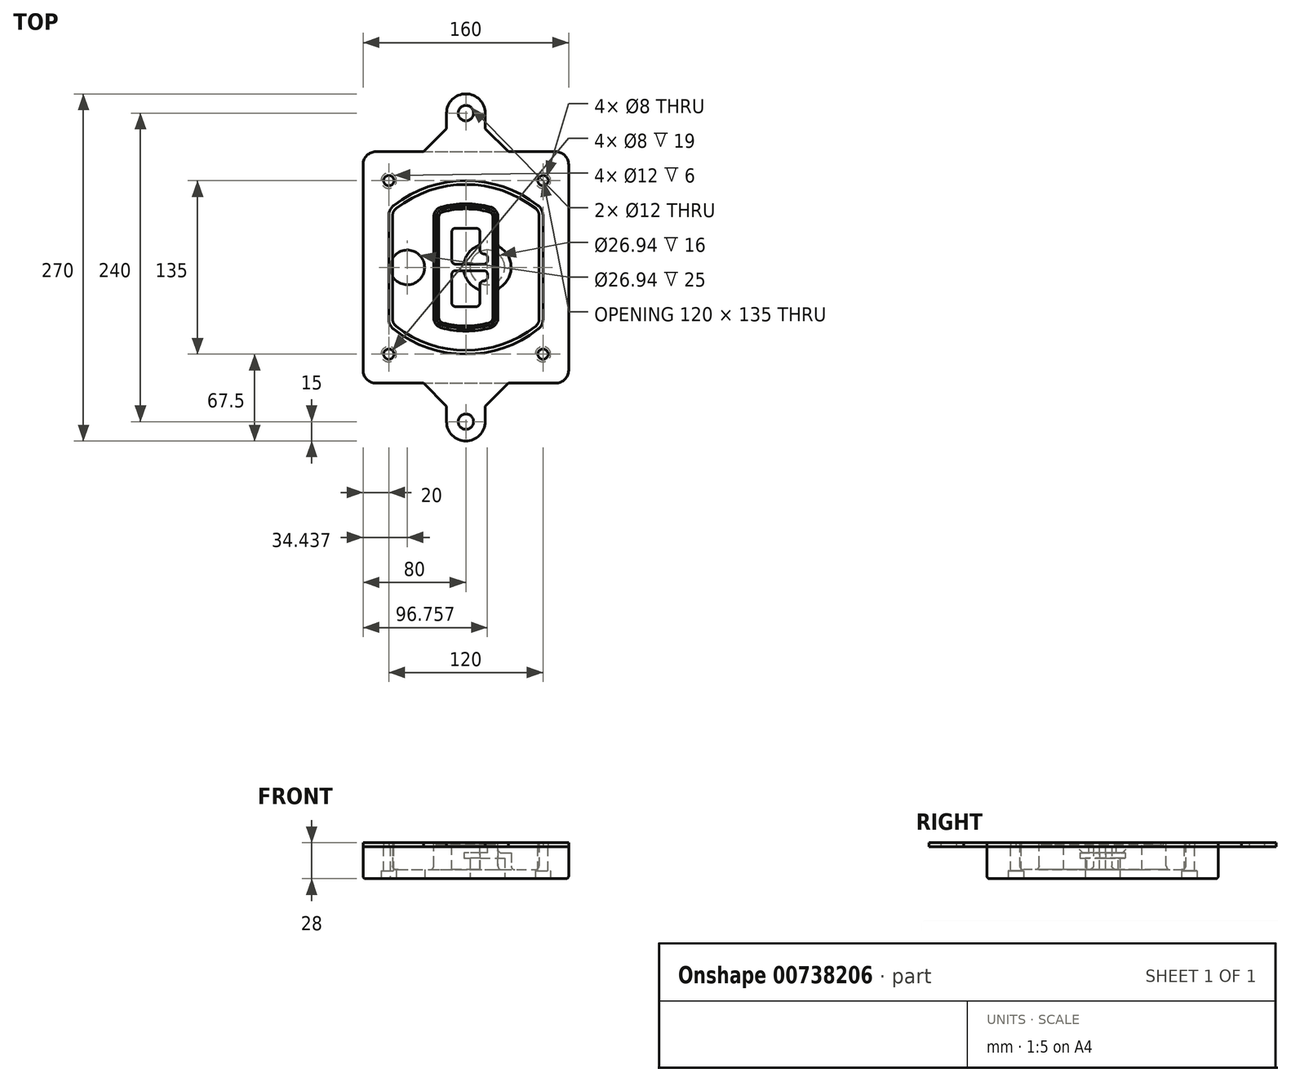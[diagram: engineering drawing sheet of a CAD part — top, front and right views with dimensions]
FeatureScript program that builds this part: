
annotation { "Feature Type Name" : "Feature", "Feature Type Description" : "" }
export const myFeature = defineFeature(function(context is Context, id is Id, definition is map)
    precondition{}
    {
        {
            var Q0;
            Q0=qCreatedBy(makeId("Top.planeOp"),FACE);
            var sketch = newSketch(context, id + "F0", { "sketchPlane" : qUnion([Q0])});
            skPoint(sketch, "E0.rect.middle", {"position": v(0, 0) * mm});
            skLineSegment(sketch, "E1.bottom", {"start": v(-70, -90) * mm, "end": v(70, -90) * mm});
            skLineSegment(sketch, "E1.top", {"start": v(-70, 90) * mm, "end": v(70, 90) * mm});
            skLineSegment(sketch, "E1.left", {"start": v(-80, -80) * mm, "end": v(-80, 80) * mm});
            skLineSegment(sketch, "E1.right", {"start": v(80, -80) * mm, "end": v(80, 80) * mm});
            skLineSegment(sketch, "E2", {"start": v(-80, 90) * mm, "end": v(80, -90) * mm, "construction": true});
            skLineSegment(sketch, "E3", {"start": v(80, 90) * mm, "end": v(-80, -90) * mm, "construction": true});
            skCircle(sketch, "E4", {"center": v(-60, 67.5) * mm, "radius": 4 * mm});
            skCircle(sketch, "E5", {"center": v(60, 67.5) * mm, "radius": 4 * mm});
            skCircle(sketch, "E6", {"center": v(60, -67.5) * mm, "radius": 4 * mm});
            skCircle(sketch, "E7", {"center": v(-60, -67.5) * mm, "radius": 4 * mm});
            skLineSegment(sketch, "E8", {"start": v(-60, 67.5) * mm, "end": v(60, 67.5) * mm, "construction": true});
            skLineSegment(sketch, "E9", {"start": v(60, 67.5) * mm, "end": v(60, -67.5) * mm, "construction": true});
            skLineSegment(sketch, "E10", {"start": v(60, -67.5) * mm, "end": v(-60, -67.5) * mm, "construction": true});
            skLineSegment(sketch, "E11", {"start": v(-60, -67.5) * mm, "end": v(-60, 67.5) * mm, "construction": true});
            skLineSegment(sketch, "E12", {"start": v(-60, 40.3) * mm, "end": v(-60, -40.3) * mm});
            skLineSegment(sketch, "E13", {"start": v(60, 40.3) * mm, "end": v(60, -40.3) * mm});
            skArc(sketch, "E14", {"start": v(56.15, 48.18) * mm, "mid": v(0, 67.5) * mm, "end": v(-56.15, 48.18) * mm});
            skArc(sketch, "E15", {"start": v(-56.15, -48.18) * mm, "mid": v(0, -67.5) * mm, "end": v(56.15, -48.18) * mm});
            skLineSegment(sketch, "E16", {"start": v(-60, 0) * mm, "end": v(60, 0) * mm, "construction": true});
            skPoint(sketch, "E17.visualSharp", {"position": v(-60, -45) * mm});
            skArc(sketch, "E17.filletArc", {"start": v(-60, -40.3) * mm, "mid": v(-58.99, -44.68) * mm, "end": v(-56.15, -48.18) * mm});
            skPoint(sketch, "E18.visualSharp", {"position": v(-60, 45) * mm});
            skArc(sketch, "E18.filletArc", {"start": v(-56.15, 48.18) * mm, "mid": v(-58.99, 44.68) * mm, "end": v(-60, 40.3) * mm});
            skPoint(sketch, "E19.visualSharp", {"position": v(60, 45) * mm});
            skArc(sketch, "E19.filletArc", {"start": v(60, 40.3) * mm, "mid": v(58.99, 44.68) * mm, "end": v(56.15, 48.18) * mm});
            skPoint(sketch, "E20.visualSharp", {"position": v(60, -45) * mm});
            skArc(sketch, "E20.filletArc", {"start": v(56.15, -48.18) * mm, "mid": v(58.99, -44.68) * mm, "end": v(60, -40.3) * mm});
            skPoint(sketch, "E21.visualSharp", {"position": v(-80, 90) * mm});
            skArc(sketch, "E21.filletArc", {"start": v(-70, 90) * mm, "mid": v(-77.07, 87.07) * mm, "end": v(-80, 80) * mm});
            skPoint(sketch, "E22.visualSharp", {"position": v(80, 90) * mm});
            skArc(sketch, "E22.filletArc", {"start": v(80, 80) * mm, "mid": v(77.07, 87.07) * mm, "end": v(70, 90) * mm});
            skPoint(sketch, "E23.visualSharp", {"position": v(80, -90) * mm});
            skArc(sketch, "E23.filletArc", {"start": v(70, -90) * mm, "mid": v(77.07, -87.07) * mm, "end": v(80, -80) * mm});
            skPoint(sketch, "E24.visualSharp", {"position": v(-80, -90) * mm});
            skArc(sketch, "E24.filletArc", {"start": v(-80, -80) * mm, "mid": v(-77.07, -87.07) * mm, "end": v(-70, -90) * mm});
            skArc(sketch, "E25.0", {"start": v(57, 40.3) * mm, "mid": v(56.3, 43.36) * mm, "end": v(54.3, 45.81) * mm});
            skLineSegment(sketch, "E25.1", {"start": v(57, 40.3) * mm, "end": v(57, -40.3) * mm});
            skArc(sketch, "E25.2", {"start": v(54.3, -45.81) * mm, "mid": v(56.3, -43.36) * mm, "end": v(57, -40.3) * mm});
            skArc(sketch, "E25.3", {"start": v(-54.3, -45.81) * mm, "mid": v(0, -64.5) * mm, "end": v(54.3, -45.81) * mm});
            skArc(sketch, "E25.4", {"start": v(-57, -40.3) * mm, "mid": v(-56.3, -43.36) * mm, "end": v(-54.3, -45.81) * mm});
            skArc(sketch, "E25.5", {"start": v(54.3, 45.81) * mm, "mid": v(0, 64.5) * mm, "end": v(-54.3, 45.81) * mm});
            skLineSegment(sketch, "E25.6", {"start": v(-57, 40.3) * mm, "end": v(-57, -40.3) * mm});
            skArc(sketch, "E25.7", {"start": v(-54.3, 45.81) * mm, "mid": v(-56.3, 43.36) * mm, "end": v(-57, 40.3) * mm});
            skArc(sketch, "E26.0", {"start": v(-58.62, 51.33) * mm, "mid": v(-62.58, 46.43) * mm, "end": v(-64, 40.3) * mm});
            skArc(sketch, "E26.1", {"start": v(58.62, 51.33) * mm, "mid": v(0, 71.5) * mm, "end": v(-58.62, 51.33) * mm});
            skArc(sketch, "E26.2", {"start": v(64, 40.3) * mm, "mid": v(62.58, 46.43) * mm, "end": v(58.62, 51.33) * mm});
            skLineSegment(sketch, "E26.3", {"start": v(64, 40.3) * mm, "end": v(64, -40.3) * mm});
            skArc(sketch, "E26.4", {"start": v(58.62, -51.33) * mm, "mid": v(62.58, -46.43) * mm, "end": v(64, -40.3) * mm});
            skLineSegment(sketch, "E26.5", {"start": v(-64, 40.3) * mm, "end": v(-64, -40.3) * mm});
            skArc(sketch, "E26.6", {"start": v(-58.62, -51.33) * mm, "mid": v(0, -71.5) * mm, "end": v(58.62, -51.33) * mm});
            skArc(sketch, "E26.7", {"start": v(-64, -40.3) * mm, "mid": v(-62.58, -46.43) * mm, "end": v(-58.62, -51.33) * mm});
            skSolve(sketch);
        }
        {
            var Q0;
            Q0=makeQuery(id+"F0.imprint","IMPRINT",FACE,{"disambiguationData":[TD([[makeQuery(id+"F0.imprint","IMPRINT",EDGE,{"derivedFrom":sQuery(id+"F0.wireOp",EDGE,"E1.bottom")}),1.0]])]});
            var Q1;
            Q1=makeQuery(id+"F0.imprint","IMPRINT",FACE,{"disambiguationData":[TD([[makeQuery(id+"F0.imprint","IMPRINT",EDGE,{"derivedFrom":sQuery(id+"F0.wireOp",EDGE,"E12")}),1.0]])]});
            var Q2;
            Q2=makeQuery(id+"F0.imprint","IMPRINT",FACE,{"disambiguationData":[TD([[makeQuery(id+"F0.imprint","IMPRINT",EDGE,{"derivedFrom":sQuery(id+"F0.wireOp",EDGE,"E25.0")}),1.0]])]});
            var Q3;
            Q3=makeQuery(id+"F0.imprint","IMPRINT",FACE,{"disambiguationData":[TD([[makeQuery(id+"F0.imprint","IMPRINT",EDGE,{"derivedFrom":sQuery(id+"F0.wireOp",EDGE,"E12")}),-1.0]])]});
            extrude(context, id + "F1", {"entities" : qUnion([Q0, Q1, Q2, Q3]), "oppositeDirection" : true, "depth" : 25 * mm});
        }
        {
            var Q0;
            Q0=makeQuery(id+"F0.imprint","IMPRINT",FACE,{"disambiguationData":[TD([[makeQuery(id+"F0.imprint","IMPRINT",EDGE,{"derivedFrom":sQuery(id+"F0.wireOp",EDGE,"E12")}),1.0]])]});
            extrude(context, id + "F2", {"entities" : qUnion([Q0]), "operationType" : NewBodyOperationType.ADD, "depth" : 3 * mm, "offsetDistance" : 25 * mm});
        }
        {
            var Q0;
            Q0=makeQuery(id+"F0.imprint","IMPRINT",FACE,{"disambiguationData":[TD([[makeQuery(id+"F0.imprint","IMPRINT",EDGE,{"derivedFrom":sQuery(id+"F0.wireOp",EDGE,"E25.0")}),1.0]])]});
            extrude(context, id + "F3", {"entities" : qUnion([Q0]), "operationType" : NewBodyOperationType.REMOVE, "oppositeDirection" : true, "depth" : 18 * mm});
        }
        {
            var Q0;
            Q0=makeQuery(id+"F2.opExtrude","CAP_FACE",FACE,{"disambiguationData":[OSD([sQuery(id+"F0.wireOp",EDGE,"E12"),sQuery(id+"F0.wireOp",EDGE,"E13"),sQuery(id+"F0.wireOp",EDGE,"E14"),sQuery(id+"F0.wireOp",EDGE,"E15"),sQuery(id+"F0.wireOp",EDGE,"E17.filletArc"),sQuery(id+"F0.wireOp",EDGE,"E18.filletArc"),sQuery(id+"F0.wireOp",EDGE,"E19.filletArc"),sQuery(id+"F0.wireOp",EDGE,"E20.filletArc"),sQuery(id+"F0.wireOp",EDGE,"E25.0"),sQuery(id+"F0.wireOp",EDGE,"E25.1"),sQuery(id+"F0.wireOp",EDGE,"E25.2"),sQuery(id+"F0.wireOp",EDGE,"E25.3"),sQuery(id+"F0.wireOp",EDGE,"E25.4"),sQuery(id+"F0.wireOp",EDGE,"E25.5"),sQuery(id+"F0.wireOp",EDGE,"E25.6"),sQuery(id+"F0.wireOp",EDGE,"E25.7")])],"isStart":false});
            var sketch = newSketch(context, id + "F4", { "sketchPlane" : qUnion([Q0])});
            skArc(sketch, "E27.0", {"start": v(-19.08, -46.97) * mm, "mid": v(0, -49.5) * mm, "end": v(19.08, -46.97) * mm});
            skArc(sketch, "E28.0", {"start": v(19.08, 46.97) * mm, "mid": v(0, 49.5) * mm, "end": v(-19.08, 46.97) * mm});
            skLineSegment(sketch, "E29", {"start": v(-25, 39.25) * mm, "end": v(-25, -39.25) * mm});
            skLineSegment(sketch, "E30", {"start": v(25, 39.25) * mm, "end": v(25, -39.25) * mm});
            skLineSegment(sketch, "E31", {"start": v(-25, 45.1) * mm, "end": v(25, 45.1) * mm, "construction": true});
            skLineSegment(sketch, "E32", {"start": v(-25, -45.1) * mm, "end": v(25, -45.1) * mm, "construction": true});
            skPoint(sketch, "E33.visualSharp", {"position": v(-25, 45.1) * mm});
            skArc(sketch, "E33.filletArc", {"start": v(-19.08, 46.97) * mm, "mid": v(-23.35, 44.11) * mm, "end": v(-25, 39.25) * mm});
            skPoint(sketch, "E34.visualSharp", {"position": v(25, 45.1) * mm});
            skArc(sketch, "E34.filletArc", {"start": v(25, 39.25) * mm, "mid": v(23.35, 44.11) * mm, "end": v(19.08, 46.97) * mm});
            skPoint(sketch, "E35.visualSharp", {"position": v(25, -45.1) * mm});
            skArc(sketch, "E35.filletArc", {"start": v(19.08, -46.97) * mm, "mid": v(23.35, -44.11) * mm, "end": v(25, -39.25) * mm});
            skPoint(sketch, "E36.visualSharp", {"position": v(-25, -45.1) * mm});
            skArc(sketch, "E36.filletArc", {"start": v(-25, -39.25) * mm, "mid": v(-23.35, -44.11) * mm, "end": v(-19.08, -46.97) * mm});
            skArc(sketch, "E37.0", {"start": v(54.3, 45.81) * mm, "mid": v(0, 64.5) * mm, "end": v(-54.3, 45.81) * mm});
            skArc(sketch, "E37.1", {"start": v(-54.3, 45.81) * mm, "mid": v(-56.3, 43.36) * mm, "end": v(-57, 40.3) * mm});
            skLineSegment(sketch, "E37.2", {"start": v(-57, 40.3) * mm, "end": v(-57, -40.3) * mm});
            skArc(sketch, "E37.3", {"start": v(-57, -40.3) * mm, "mid": v(-56.3, -43.36) * mm, "end": v(-54.3, -45.81) * mm});
            skArc(sketch, "E37.4", {"start": v(-54.3, -45.81) * mm, "mid": v(0, -64.5) * mm, "end": v(54.3, -45.81) * mm});
            skArc(sketch, "E37.5", {"start": v(54.3, -45.81) * mm, "mid": v(56.3, -43.36) * mm, "end": v(57, -40.3) * mm});
            skLineSegment(sketch, "E37.6", {"start": v(57, 40.3) * mm, "end": v(57, -40.3) * mm});
            skArc(sketch, "E37.7", {"start": v(57, 40.3) * mm, "mid": v(56.3, 43.36) * mm, "end": v(54.3, 45.81) * mm});
            skLineSegment(sketch, "E38.0", {"start": v(23, 39.25) * mm, "end": v(23, -39.25) * mm});
            skArc(sketch, "E38.1", {"start": v(18.56, -45.04) * mm, "mid": v(21.76, -42.9) * mm, "end": v(23, -39.25) * mm});
            skArc(sketch, "E38.2", {"start": v(-18.56, -45.04) * mm, "mid": v(0, -47.5) * mm, "end": v(18.56, -45.04) * mm});
            skArc(sketch, "E38.3", {"start": v(-23, -39.25) * mm, "mid": v(-21.76, -42.9) * mm, "end": v(-18.56, -45.04) * mm});
            skLineSegment(sketch, "E38.4", {"start": v(-23, 39.25) * mm, "end": v(-23, -39.25) * mm});
            skArc(sketch, "E38.5", {"start": v(23, 39.25) * mm, "mid": v(21.76, 42.9) * mm, "end": v(18.56, 45.04) * mm});
            skArc(sketch, "E38.6", {"start": v(-18.56, 45.04) * mm, "mid": v(-21.76, 42.9) * mm, "end": v(-23, 39.25) * mm});
            skArc(sketch, "E38.7", {"start": v(18.56, 45.04) * mm, "mid": v(0, 47.5) * mm, "end": v(-18.56, 45.04) * mm});
            skArc(sketch, "E39.0", {"start": v(21, 39.25) * mm, "mid": v(20.18, 41.68) * mm, "end": v(18.04, 43.1) * mm});
            skLineSegment(sketch, "E39.1", {"start": v(21, 39.25) * mm, "end": v(21, -39.25) * mm});
            skArc(sketch, "E39.2", {"start": v(18.04, -43.1) * mm, "mid": v(20.18, -41.68) * mm, "end": v(21, -39.25) * mm});
            skArc(sketch, "E39.3", {"start": v(-18.04, -43.1) * mm, "mid": v(0, -45.5) * mm, "end": v(18.04, -43.1) * mm});
            skArc(sketch, "E39.4", {"start": v(-21, -39.25) * mm, "mid": v(-20.18, -41.68) * mm, "end": v(-18.04, -43.1) * mm});
            skArc(sketch, "E39.5", {"start": v(18.04, 43.1) * mm, "mid": v(0, 45.5) * mm, "end": v(-18.04, 43.1) * mm});
            skLineSegment(sketch, "E39.6", {"start": v(-21, 39.25) * mm, "end": v(-21, -39.25) * mm});
            skArc(sketch, "E39.7", {"start": v(-18.04, 43.1) * mm, "mid": v(-20.18, 41.68) * mm, "end": v(-21, 39.25) * mm});
            skLineSegment(sketch, "E40", {"start": v(-25, 0) * mm, "end": v(25, 0) * mm, "construction": true});
            skLineSegment(sketch, "E41", {"start": v(-11, 5.5) * mm, "end": v(-11, 27.5) * mm});
            skLineSegment(sketch, "E42", {"start": v(-8, 30.5) * mm, "end": v(8, 30.5) * mm});
            skLineSegment(sketch, "E43", {"start": v(11, 27.5) * mm, "end": v(11, 13.5) * mm});
            skLineSegment(sketch, "E44", {"start": v(14, 10.5) * mm, "end": v(14, 10.5) * mm});
            skLineSegment(sketch, "E45", {"start": v(17, 7.5) * mm, "end": v(17, 5.5) * mm});
            skLineSegment(sketch, "E46", {"start": v(14, 2.5) * mm, "end": v(-8, 2.5) * mm});
            skPoint(sketch, "E47.visualSharp", {"position": v(-11, 30.5) * mm});
            skArc(sketch, "E47.filletArc", {"start": v(-8, 30.5) * mm, "mid": v(-10.12, 29.62) * mm, "end": v(-11, 27.5) * mm});
            skPoint(sketch, "E48.visualSharp", {"position": v(11, 30.5) * mm});
            skArc(sketch, "E48.filletArc", {"start": v(11, 27.5) * mm, "mid": v(10.12, 29.62) * mm, "end": v(8, 30.5) * mm});
            skPoint(sketch, "E49.visualSharp", {"position": v(11, 10.5) * mm});
            skArc(sketch, "E49.filletArc", {"start": v(11, 13.5) * mm, "mid": v(11.88, 11.38) * mm, "end": v(14, 10.5) * mm});
            skPoint(sketch, "E50.visualSharp", {"position": v(17, 10.5) * mm});
            skArc(sketch, "E50.filletArc", {"start": v(17, 7.5) * mm, "mid": v(16.12, 9.62) * mm, "end": v(14, 10.5) * mm});
            skPoint(sketch, "E51.visualSharp", {"position": v(17, 2.5) * mm});
            skArc(sketch, "E51.filletArc", {"start": v(14, 2.5) * mm, "mid": v(16.12, 3.38) * mm, "end": v(17, 5.5) * mm});
            skPoint(sketch, "E52.visualSharp", {"position": v(-11, 2.5) * mm});
            skArc(sketch, "E52.filletArc", {"start": v(-11, 5.5) * mm, "mid": v(-10.12, 3.38) * mm, "end": v(-8, 2.5) * mm});
            skLineSegment(sketch, "E53.0.MirrorCS", {"start": v(14, -2.5) * mm, "end": v(-8, -2.5) * mm});
            skArc(sketch, "E54.0.MirrorCS", {"start": v(-11, -5.5) * mm, "mid": v(-10.12, -3.38) * mm, "end": v(-8, -2.5) * mm});
            skLineSegment(sketch, "E55.0.MirrorCS", {"start": v(-11, -5.5) * mm, "end": v(-11, -27.5) * mm});
            skArc(sketch, "E56.0.MirrorCS", {"start": v(-8, -30.5) * mm, "mid": v(-10.12, -29.62) * mm, "end": v(-11, -27.5) * mm});
            skLineSegment(sketch, "E57.0.MirrorCS", {"start": v(-8, -30.5) * mm, "end": v(8, -30.5) * mm});
            skArc(sketch, "E58.0.MirrorCS", {"start": v(11, -27.5) * mm, "mid": v(10.12, -29.62) * mm, "end": v(8, -30.5) * mm});
            skLineSegment(sketch, "E59.0.MirrorCS", {"start": v(11, -27.5) * mm, "end": v(11, -13.5) * mm});
            skArc(sketch, "E60.0.MirrorCS", {"start": v(11, -13.5) * mm, "mid": v(11.88, -11.38) * mm, "end": v(14, -10.5) * mm});
            skArc(sketch, "E61.0.MirrorCS", {"start": v(17, -7.5) * mm, "mid": v(16.12, -9.62) * mm, "end": v(14, -10.5) * mm});
            skLineSegment(sketch, "E62.0.MirrorCS", {"start": v(17, -7.5) * mm, "end": v(17, -5.5) * mm});
            skArc(sketch, "E63.0.MirrorCS", {"start": v(14, -2.5) * mm, "mid": v(16.12, -3.38) * mm, "end": v(17, -5.5) * mm});
            skSolve(sketch);
        }
        {
            var Q0;
            Q0=makeQuery(id+"F4.imprint","IMPRINT",FACE,{"disambiguationData":[TD([[makeQuery(id+"F4.imprint","IMPRINT",EDGE,{"derivedFrom":sQuery(id+"F4.wireOp",EDGE,"E27.0")}),1.0]])]});
            var Q1;
            Q1=makeQuery(id+"F4.imprint","IMPRINT",FACE,{"disambiguationData":[TD([[makeQuery(id+"F4.imprint","IMPRINT",EDGE,{"derivedFrom":sQuery(id+"F4.wireOp",EDGE,"E38.0")}),-1.0]])]});
            var Q2;
            Q2=makeQuery(id+"F4.imprint","IMPRINT",FACE,{"disambiguationData":[TD([[makeQuery(id+"F4.imprint","IMPRINT",EDGE,{"derivedFrom":sQuery(id+"F4.wireOp",EDGE,"E39.0")}),1.0]])]});
            extrude(context, id + "F5", {"entities" : qUnion([Q0, Q1, Q2]), "operationType" : NewBodyOperationType.ADD, "endBound" : BoundingType.UP_TO_NEXT, "oppositeDirection" : true, "depth" : 25 * mm});
        }
        {
            var Q0;
            Q0=makeQuery(id+"F4.imprint","IMPRINT",FACE,{"disambiguationData":[TD([[makeQuery(id+"F4.imprint","IMPRINT",EDGE,{"derivedFrom":sQuery(id+"F4.wireOp",EDGE,"E38.0")}),-1.0]])]});
            extrude(context, id + "F6", {"entities" : qUnion([Q0]), "operationType" : NewBodyOperationType.REMOVE, "oppositeDirection" : true, "depth" : 2 * mm});
        }
        {
            var Q0;
            Q0=makeQuery(id+"F1.opExtrude","CAP_FACE",FACE,{"disambiguationData":[OSD([sQuery(id+"F0.wireOp",EDGE,"E1.bottom"),sQuery(id+"F0.wireOp",EDGE,"E1.top"),sQuery(id+"F0.wireOp",EDGE,"E1.left"),sQuery(id+"F0.wireOp",EDGE,"E1.right"),sQuery(id+"F0.wireOp",EDGE,"E4"),sQuery(id+"F0.wireOp",EDGE,"E5"),sQuery(id+"F0.wireOp",EDGE,"E6"),sQuery(id+"F0.wireOp",EDGE,"E7"),sQuery(id+"F0.wireOp",EDGE,"E21.filletArc"),sQuery(id+"F0.wireOp",EDGE,"E22.filletArc"),sQuery(id+"F0.wireOp",EDGE,"E23.filletArc"),sQuery(id+"F0.wireOp",EDGE,"E24.filletArc")])],"isStart":false});
            var sketch = newSketch(context, id + "F7", { "sketchPlane" : qUnion([Q0])});
            skCircle(sketch, "E64", {"center": v(16.76, 0) * mm, "radius": 13.47 * mm});
            skCircle(sketch, "E65", {"center": v(-45.56, 0) * mm, "radius": 13.47 * mm});
            skLineSegment(sketch, "E66", {"start": v(80, 0) * mm, "end": v(-80, 0) * mm});
            skCircle(sketch, "E67", {"center": v(16.76, 0) * mm, "radius": 18.47 * mm});
            skCircle(sketch, "E68", {"center": v(60, -67.5) * mm, "radius": 6 * mm});
            skCircle(sketch, "E69", {"center": v(-60, -67.5) * mm, "radius": 6 * mm});
            skCircle(sketch, "E70", {"center": v(-60, 67.5) * mm, "radius": 6 * mm});
            skCircle(sketch, "E71", {"center": v(60, 67.5) * mm, "radius": 6 * mm});
            skSolve(sketch);
        }
        {
            var Q0;
            {var subQ1=sQuery(id+"F7.wireOp",EDGE,"E66");var subQ4=sQuery(id+"F7.wireOp",EDGE,"E64");var subQ6=makeQuery(id+"F7.imprint","INTERSECT",VERTEX,{"disambiguationData":[OD(0.0)],"derivedFrom":[subQ4,subQ1]});Q0=makeQuery(id+"F7.imprint","IMPRINT",FACE,{"disambiguationData":[TD([[makeQuery(id+"F7.imprint","IMPRINT",EDGE,{"disambiguationData":[TD([[subQ6,-1.0]])],"derivedFrom":subQ4}),-1.0]])]});}
            var Q1;
            {var subQ0=sQuery(id+"F7.wireOp",EDGE,"E66");var subQ1=sQuery(id+"F7.wireOp",EDGE,"E64");var subQ3=makeQuery(id+"F7.imprint","INTERSECT",VERTEX,{"disambiguationData":[OD(0.0)],"derivedFrom":[subQ1,subQ0]});Q1=makeQuery(id+"F7.imprint","IMPRINT",FACE,{"disambiguationData":[TD([[makeQuery(id+"F7.imprint","IMPRINT",EDGE,{"disambiguationData":[TD([[subQ3,-1.0]])],"derivedFrom":subQ1}),1.0]])]});}
            var Q2;
            {var subQ0=sQuery(id+"F7.wireOp",EDGE,"E66");var subQ1=sQuery(id+"F7.wireOp",EDGE,"E64");var subQ3=makeQuery(id+"F7.imprint","INTERSECT",VERTEX,{"disambiguationData":[OD(0.0)],"derivedFrom":[subQ1,subQ0]});Q2=makeQuery(id+"F7.imprint","IMPRINT",FACE,{"disambiguationData":[TD([[makeQuery(id+"F7.imprint","IMPRINT",EDGE,{"disambiguationData":[TD([[subQ3,1.0]])],"derivedFrom":subQ1}),1.0]])]});}
            var Q3;
            {var subQ1=sQuery(id+"F7.wireOp",EDGE,"E66");var subQ4=sQuery(id+"F7.wireOp",EDGE,"E64");var subQ6=makeQuery(id+"F7.imprint","INTERSECT",VERTEX,{"disambiguationData":[OD(0.0)],"derivedFrom":[subQ4,subQ1]});Q3=makeQuery(id+"F7.imprint","IMPRINT",FACE,{"disambiguationData":[TD([[makeQuery(id+"F7.imprint","IMPRINT",EDGE,{"disambiguationData":[TD([[subQ6,1.0]])],"derivedFrom":subQ4}),-1.0]])]});}
            extrude(context, id + "F8", {"entities" : qUnion([Q0, Q1, Q2, Q3]), "operationType" : NewBodyOperationType.ADD, "oppositeDirection" : true, "depth" : 20 * mm});
        }
        {
            var Q0;
            {var subQ0=sQuery(id+"F7.wireOp",EDGE,"E66");var subQ1=sQuery(id+"F7.wireOp",EDGE,"E64");var subQ3=makeQuery(id+"F7.imprint","INTERSECT",VERTEX,{"disambiguationData":[OD(0.0)],"derivedFrom":[subQ1,subQ0]});Q0=makeQuery(id+"F7.imprint","IMPRINT",FACE,{"disambiguationData":[TD([[makeQuery(id+"F7.imprint","IMPRINT",EDGE,{"disambiguationData":[TD([[subQ3,-1.0]])],"derivedFrom":subQ1}),1.0]])]});}
            var Q1;
            {var subQ0=sQuery(id+"F7.wireOp",EDGE,"E66");var subQ1=sQuery(id+"F7.wireOp",EDGE,"E64");var subQ3=makeQuery(id+"F7.imprint","INTERSECT",VERTEX,{"disambiguationData":[OD(0.0)],"derivedFrom":[subQ1,subQ0]});Q1=makeQuery(id+"F7.imprint","IMPRINT",FACE,{"disambiguationData":[TD([[makeQuery(id+"F7.imprint","IMPRINT",EDGE,{"disambiguationData":[TD([[subQ3,1.0]])],"derivedFrom":subQ1}),1.0]])]});}
            extrude(context, id + "F9", {"entities" : qUnion([Q0, Q1]), "operationType" : NewBodyOperationType.REMOVE, "oppositeDirection" : true, "depth" : 16 * mm});
        }
        {
            var Q0;
            {var subQ0=sQuery(id+"F7.wireOp",EDGE,"E66");var subQ1=sQuery(id+"F7.wireOp",EDGE,"E65");var subQ3=makeQuery(id+"F7.imprint","INTERSECT",VERTEX,{"disambiguationData":[OD(0.0)],"derivedFrom":[subQ1,subQ0]});Q0=makeQuery(id+"F7.imprint","IMPRINT",FACE,{"disambiguationData":[TD([[makeQuery(id+"F7.imprint","IMPRINT",EDGE,{"disambiguationData":[TD([[subQ3,-1.0]])],"derivedFrom":subQ1}),1.0]])]});}
            var Q1;
            {var subQ0=sQuery(id+"F7.wireOp",EDGE,"E66");var subQ1=sQuery(id+"F7.wireOp",EDGE,"E65");var subQ3=makeQuery(id+"F7.imprint","INTERSECT",VERTEX,{"disambiguationData":[OD(0.0)],"derivedFrom":[subQ1,subQ0]});Q1=makeQuery(id+"F7.imprint","IMPRINT",FACE,{"disambiguationData":[TD([[makeQuery(id+"F7.imprint","IMPRINT",EDGE,{"disambiguationData":[TD([[subQ3,1.0]])],"derivedFrom":subQ1}),1.0]])]});}
            extrude(context, id + "F10", {"entities" : qUnion([Q0, Q1]), "operationType" : NewBodyOperationType.REMOVE, "oppositeDirection" : true, "depth" : 25 * mm});
        }
        {
            var Q0;
            Q0=makeQuery(id+"F7.imprint","IMPRINT",FACE,{"disambiguationData":[TD([[makeQuery(id+"F7.imprint","IMPRINT",EDGE,{"derivedFrom":sQuery(id+"F7.wireOp",EDGE,"E68")}),1.0]])]});
            var Q1;
            Q1=makeQuery(id+"F7.imprint","IMPRINT",FACE,{"disambiguationData":[TD([[makeQuery(id+"F7.imprint","IMPRINT",EDGE,{"derivedFrom":makeQuery(id+"F1.opExtrude","CAP_EDGE",EDGE,{"disambiguationData":[OSD([sQuery(id+"F0.wireOp",EDGE,"E5")])],"isStart":false})}),-1.0]])]});
            var Q2;
            Q2=makeQuery(id+"F7.imprint","IMPRINT",FACE,{"disambiguationData":[TD([[makeQuery(id+"F7.imprint","IMPRINT",EDGE,{"derivedFrom":sQuery(id+"F7.wireOp",EDGE,"E69")}),1.0]])]});
            var Q3;
            Q3=makeQuery(id+"F7.imprint","IMPRINT",FACE,{"disambiguationData":[TD([[makeQuery(id+"F7.imprint","IMPRINT",EDGE,{"derivedFrom":makeQuery(id+"F1.opExtrude","CAP_EDGE",EDGE,{"disambiguationData":[OSD([sQuery(id+"F0.wireOp",EDGE,"E4")])],"isStart":false})}),-1.0]])]});
            var Q4;
            Q4=makeQuery(id+"F7.imprint","IMPRINT",FACE,{"disambiguationData":[TD([[makeQuery(id+"F7.imprint","IMPRINT",EDGE,{"derivedFrom":sQuery(id+"F7.wireOp",EDGE,"E70")}),1.0]])]});
            var Q5;
            Q5=makeQuery(id+"F7.imprint","IMPRINT",FACE,{"disambiguationData":[TD([[makeQuery(id+"F7.imprint","IMPRINT",EDGE,{"derivedFrom":makeQuery(id+"F1.opExtrude","CAP_EDGE",EDGE,{"disambiguationData":[OSD([sQuery(id+"F0.wireOp",EDGE,"E7")])],"isStart":false})}),-1.0]])]});
            var Q6;
            Q6=makeQuery(id+"F7.imprint","IMPRINT",FACE,{"disambiguationData":[TD([[makeQuery(id+"F7.imprint","IMPRINT",EDGE,{"derivedFrom":sQuery(id+"F7.wireOp",EDGE,"E71")}),1.0]])]});
            var Q7;
            Q7=makeQuery(id+"F7.imprint","IMPRINT",FACE,{"disambiguationData":[TD([[makeQuery(id+"F7.imprint","IMPRINT",EDGE,{"derivedFrom":makeQuery(id+"F1.opExtrude","CAP_EDGE",EDGE,{"disambiguationData":[OSD([sQuery(id+"F0.wireOp",EDGE,"E6")])],"isStart":false})}),-1.0]])]});
            extrude(context, id + "F11", {"entities" : qUnion([Q0, Q1, Q2, Q3, Q4, Q5, Q6, Q7]), "operationType" : NewBodyOperationType.REMOVE, "oppositeDirection" : true, "depth" : 6 * mm});
        }
        {
            var Q0;
            Q0=makeQuery(id+"F9.boolean.opBoolean","COPY",FACE,{"derivedFrom":makeQuery(id+"F9.opExtrude","CAP_FACE",FACE,{"disambiguationData":[OSD([sQuery(id+"F7.wireOp",EDGE,"E64")])],"isStart":false})});
            var sketch = newSketch(context, id + "F12", { "sketchPlane" : qUnion([Q0])});
            skArc(sketch, "E72.0", {"start": v(11, 17.55) * mm, "mid": v(2.57, 11.82) * mm, "end": v(-1.54, 2.5) * mm});
            skArc(sketch, "E72.1", {"start": v(-1.54, -2.5) * mm, "mid": v(2.57, -11.82) * mm, "end": v(11, -17.55) * mm});
            skLineSegment(sketch, "E73", {"start": v(-1.54, -2.5) * mm, "end": v(14, -2.5) * mm});
            skLineSegment(sketch, "E74.0", {"start": v(14, 2.5) * mm, "end": v(-1.54, 2.5) * mm});
            skArc(sketch, "E74.1", {"start": v(14, 2.5) * mm, "mid": v(16.12, 3.38) * mm, "end": v(17, 5.5) * mm});
            skLineSegment(sketch, "E74.2", {"start": v(17, 7.5) * mm, "end": v(17, 5.5) * mm});
            skArc(sketch, "E74.3", {"start": v(17, 7.5) * mm, "mid": v(16.12, 9.62) * mm, "end": v(14, 10.5) * mm});
            skArc(sketch, "E74.4", {"start": v(11, 13.5) * mm, "mid": v(11.88, 11.38) * mm, "end": v(14, 10.5) * mm});
            skLineSegment(sketch, "E74.5", {"start": v(11, 17.55) * mm, "end": v(11, 13.5) * mm});
            skLineSegment(sketch, "E74.7", {"start": v(14, -2.5) * mm, "end": v(-1.54, -2.5) * mm});
            skArc(sketch, "E74.8", {"start": v(14, -2.5) * mm, "mid": v(16.12, -3.38) * mm, "end": v(17, -5.5) * mm});
            skLineSegment(sketch, "E74.9", {"start": v(17, -7.5) * mm, "end": v(17, -5.5) * mm});
            skArc(sketch, "E74.10", {"start": v(17, -7.5) * mm, "mid": v(16.12, -9.62) * mm, "end": v(14, -10.5) * mm});
            skArc(sketch, "E74.11", {"start": v(11, -13.5) * mm, "mid": v(11.88, -11.38) * mm, "end": v(14, -10.5) * mm});
            skLineSegment(sketch, "E74.12", {"start": v(11, -17.55) * mm, "end": v(11, -13.5) * mm});
            skPoint(sketch, "E75.orphan", {"position": v(11, -27.5) * mm});
            skPoint(sketch, "E76.orphan", {"position": v(-8, -2.5) * mm});
            skPoint(sketch, "E77.orphan", {"position": v(-8, 2.5) * mm});
            skPoint(sketch, "E78.orphan", {"position": v(11, 27.5) * mm});
            skSolve(sketch);
        }
        {
            var Q0;
            {var subQ7=sQuery(id+"F12.wireOp",EDGE,"E72.0");var subQ14=sQuery(id+"F12.wireOp",EDGE,"E72.1");var subQ16=sQuery(id+"F12.wireOp",EDGE,"E74.1");var subQ18=sQuery(id+"F12.wireOp",EDGE,"E74.8");Q0=qUnion([makeQuery(id+"F12.imprint","IMPRINT",FACE,{"disambiguationData":[TD([[makeQuery(id+"F12.imprint","IMPRINT",EDGE,{"derivedFrom":subQ7}),1.0]])]}),makeQuery(id+"F12.imprint","IMPRINT",FACE,{"disambiguationData":[TD([[makeQuery(id+"F12.imprint","IMPRINT",EDGE,{"derivedFrom":subQ14}),1.0]])]}),makeQuery(id+"F12.imprint","IMPRINT",FACE,{"disambiguationData":[TD([[makeQuery(id+"F12.imprint","IMPRINT",EDGE,{"derivedFrom":subQ16}),1.0]])]}),makeQuery(id+"F12.imprint","IMPRINT",FACE,{"disambiguationData":[TD([[makeQuery(id+"F12.imprint","IMPRINT",EDGE,{"derivedFrom":subQ18}),-1.0]])]})]);}
            var Q1;
            Q1=makeQuery(id+"F5.boolean.opBoolean","SPLIT",FACE,{"disambiguationData":[TD([makeQuery(id+"F5.opExtrude","SWEPT_FACE",FACE,{"disambiguationData":[OSD([sQuery(id+"F4.wireOp",EDGE,"E41")])]})])],"derivedFrom":makeQuery(id+"F3.boolean.opBoolean","COPY",FACE,{"derivedFrom":makeQuery(id+"F3.opExtrude","CAP_FACE",FACE,{"disambiguationData":[OSD([sQuery(id+"F0.wireOp",EDGE,"E25.0"),sQuery(id+"F0.wireOp",EDGE,"E25.1"),sQuery(id+"F0.wireOp",EDGE,"E25.2"),sQuery(id+"F0.wireOp",EDGE,"E25.3"),sQuery(id+"F0.wireOp",EDGE,"E25.4"),sQuery(id+"F0.wireOp",EDGE,"E25.5"),sQuery(id+"F0.wireOp",EDGE,"E25.6"),sQuery(id+"F0.wireOp",EDGE,"E25.7")])],"isStart":false})})});
            extrude(context, id + "F13", {"entities" : qUnion([Q0]), "operationType" : NewBodyOperationType.REMOVE, "endBound" : BoundingType.UP_TO_SURFACE, "endBoundEntityFace" : qUnion([Q1]), "depth" : 25 * mm});
        }
        {
            var Q0;
            Q0=makeQuery(id+"F3.boolean.opBoolean","COPY",EDGE,{"derivedFrom":makeQuery(id+"F3.opExtrude","CAP_EDGE",EDGE,{"disambiguationData":[OSD([sQuery(id+"F0.wireOp",EDGE,"E25.6")])],"isStart":false})});
            var Q1;
            Q1=makeQuery(id+"F8.boolean.opBoolean","INTERSECT",EDGE,{"derivedFrom":[makeQuery(id+"F5.opExtrude","SWEPT_FACE",FACE,{"disambiguationData":[OSD([sQuery(id+"F4.wireOp",EDGE,"E30")])]}),makeQuery(id+"F8.opExtrude","CAP_FACE",FACE,{"disambiguationData":[OSD([sQuery(id+"F7.wireOp",EDGE,"E67")])],"isStart":false})]});
            var Q2;
            Q2=makeQuery(id+"F8.boolean.opBoolean","INTERSECT",EDGE,{"disambiguationData":[OD(1.0)],"derivedFrom":[makeQuery(id+"F5.opExtrude","SWEPT_FACE",FACE,{"disambiguationData":[OSD([sQuery(id+"F4.wireOp",EDGE,"E30")])]}),makeQuery(id+"F8.opExtrude","SWEPT_FACE",FACE,{"disambiguationData":[OSD([sQuery(id+"F7.wireOp",EDGE,"E67")])]})]});
            var Q3;
            {var subQ0=sQuery(id+"F4.wireOp",EDGE,"E30");Q3=makeQuery(id+"F8.boolean.opBoolean","SPLIT",EDGE,{"disambiguationData":[TD([makeQuery(id+"F5.opExtrude","SWEPT_FACE",FACE,{"disambiguationData":[OSD([sQuery(id+"F4.wireOp",EDGE,"E35.filletArc")])]})])],"derivedFrom":makeQuery(id+"F5.opExtrude","CAP_EDGE",EDGE,{"disambiguationData":[OSD([subQ0])],"isStart":false})});}
            var Q4;
            {var subQ0=sQuery(id+"F0.wireOp",EDGE,"E25.7");var subQ1=sQuery(id+"F0.wireOp",EDGE,"E25.1");var subQ2=sQuery(id+"F0.wireOp",EDGE,"E25.6");var subQ3=sQuery(id+"F0.wireOp",EDGE,"E25.5");var subQ4=sQuery(id+"F0.wireOp",EDGE,"E25.4");var subQ5=sQuery(id+"F0.wireOp",EDGE,"E25.0");var subQ6=sQuery(id+"F0.wireOp",EDGE,"E25.2");var subQ7=sQuery(id+"F0.wireOp",EDGE,"E25.3");Q4=makeQuery(id+"F8.boolean.opBoolean","INTERSECT",EDGE,{"derivedFrom":[makeQuery(id+"F5.boolean.opBoolean","SPLIT",FACE,{"disambiguationData":[TD([makeQuery(id+"F2.opExtrude","SWEPT_FACE",FACE,{"disambiguationData":[OSD([subQ5])]})])],"derivedFrom":makeQuery(id+"F3.boolean.opBoolean","COPY",FACE,{"derivedFrom":makeQuery(id+"F3.opExtrude","CAP_FACE",FACE,{"disambiguationData":[OSD([subQ5,subQ1,subQ6,subQ7,subQ4,subQ3,subQ2,subQ0])],"isStart":false})})}),makeQuery(id+"F8.opExtrude","SWEPT_FACE",FACE,{"disambiguationData":[OSD([sQuery(id+"F7.wireOp",EDGE,"E67")])]})]});}
            var Q5;
            Q5=makeQuery(id+"F8.boolean.opBoolean","INTERSECT",EDGE,{"disambiguationData":[OD(0.0)],"derivedFrom":[makeQuery(id+"F5.opExtrude","SWEPT_FACE",FACE,{"disambiguationData":[OSD([sQuery(id+"F4.wireOp",EDGE,"E30")])]}),makeQuery(id+"F8.opExtrude","SWEPT_FACE",FACE,{"disambiguationData":[OSD([sQuery(id+"F7.wireOp",EDGE,"E67")])]})]});
            fillet(context, id + "F14", {"entities" : qUnion([Q0, Q1, Q2, Q3, Q4, Q5]), "radius" : 3 * mm, "tangentPropagation" : true, "allowEdgeOverflow" : false});
        }
        {
            var Q0;
            Q0=makeQuery(id+"F1.opExtrude","CAP_EDGE",EDGE,{"disambiguationData":[OSD([sQuery(id+"F0.wireOp",EDGE,"E1.bottom")])],"isStart":false});
            fillet(context, id + "F15", {"entities" : qUnion([Q0]), "radius" : 2 * mm, "tangentPropagation" : true, "allowEdgeOverflow" : false});
        }
        {
            var Q0;
            {var subQ0=sQuery(id+"F0.wireOp",EDGE,"E21.filletArc");var subQ1=sQuery(id+"F0.wireOp",EDGE,"E7");var subQ2=sQuery(id+"F0.wireOp",EDGE,"E6");var subQ3=sQuery(id+"F0.wireOp",EDGE,"E5");var subQ4=sQuery(id+"F0.wireOp",EDGE,"E4");var subQ5=sQuery(id+"F0.wireOp",EDGE,"E22.filletArc");var subQ6=sQuery(id+"F0.wireOp",EDGE,"E1.bottom");var subQ7=sQuery(id+"F0.wireOp",EDGE,"E1.right");var subQ8=sQuery(id+"F0.wireOp",EDGE,"E1.top");var subQ9=sQuery(id+"F0.wireOp",EDGE,"E1.left");var subQ10=sQuery(id+"F0.wireOp",EDGE,"E23.filletArc");var subQ11=sQuery(id+"F0.wireOp",EDGE,"E24.filletArc");Q0=makeQuery(id+"F2.boolean.opBoolean","SPLIT",FACE,{"disambiguationData":[TD([makeQuery(id+"F1.opExtrude","SWEPT_FACE",FACE,{"disambiguationData":[OSD([subQ6])]})])],"derivedFrom":makeQuery(id+"F1.opExtrude","CAP_FACE",FACE,{"disambiguationData":[OSD([subQ6,subQ8,subQ9,subQ7,subQ4,subQ3,subQ2,subQ1,subQ0,subQ5,subQ10,subQ11])],"isStart":true})});}
            var sketch = newSketch(context, id + "F16", { "sketchPlane" : qUnion([Q0])});
            skLineSegment(sketch, "E79.0", {"start": v(-70, 90) * mm, "end": v(70, 90) * mm});
            skLineSegment(sketch, "E79.1", {"start": v(-80, -80) * mm, "end": v(-80, 80) * mm});
            skLineSegment(sketch, "E79.2", {"start": v(80, -80) * mm, "end": v(80, 80) * mm});
            skPoint(sketch, "E79.4", {"position": v(-77.07, 87.07) * mm});
            skLineSegment(sketch, "E80", {"start": v(0, 0) * mm, "end": v(0, 120) * mm, "construction": true});
            skPoint(sketch, "E80.endSnap0", {"position": v(0, 67.5) * mm});
            skLineSegment(sketch, "E81", {"start": v(-33, 90) * mm, "end": v(-15, 108) * mm});
            skLineSegment(sketch, "E82", {"start": v(-15, 108) * mm, "end": v(-15, 120) * mm});
            skLineSegment(sketch, "E83", {"start": v(15.3, 90) * mm, "end": v(15, 90.3) * mm});
            skCircle(sketch, "E84", {"center": v(0, 120) * mm, "radius": 6 * mm});
            skArc(sketch, "E85", {"start": v(15, 120) * mm, "mid": v(0, 135) * mm, "end": v(-15, 120) * mm});
            skLineSegment(sketch, "E86", {"start": v(-80, 0) * mm, "end": v(80, 0) * mm, "construction": true});
            skLineSegment(sketch, "E87.MirrorCS", {"start": v(-33, -90) * mm, "end": v(-15, -108) * mm});
            skLineSegment(sketch, "E88.MirrorCS", {"start": v(-15, -108) * mm, "end": v(-15, -120) * mm});
            skArc(sketch, "E89.MirrorCS", {"start": v(15, -120) * mm, "mid": v(0, -135) * mm, "end": v(-15, -120) * mm});
            skLineSegment(sketch, "E90.MirrorCS", {"start": v(15.3, -90) * mm, "end": v(15, -90.3) * mm});
            skCircle(sketch, "E91.MirrorC", {"center": v(0, -120) * mm, "radius": 6 * mm});
            skLineSegment(sketch, "E92", {"start": v(15, 120) * mm, "end": v(15, 108) * mm});
            skLineSegment(sketch, "E93", {"start": v(15, 108) * mm, "end": v(33, 90) * mm});
            skLineSegment(sketch, "E94.MirrorCS", {"start": v(15, -108) * mm, "end": v(33, -90) * mm});
            skLineSegment(sketch, "E95.MirrorCS", {"start": v(15, -120) * mm, "end": v(15, -108) * mm});
            skSolve(sketch);
        }
        {
            var Q0;
            {var subQ1=sQuery(id+"F16.wireOp",EDGE,"E81");Q0=makeQuery(id+"F16.imprint","IMPRINT",FACE,{"disambiguationData":[TD([[makeQuery(id+"F16.imprint","IMPRINT",EDGE,{"derivedFrom":subQ1}),-1.0]])]});}
            var Q1;
            Q1=makeQuery(id+"F16.imprint","IMPRINT",FACE,{"disambiguationData":[TD([[makeQuery(id+"F16.imprint","IMPRINT",EDGE,{"derivedFrom":sQuery(id+"F16.wireOp",EDGE,"E79.1")}),-1.0]])]});
            var Q2;
            {var subQ1=sQuery(id+"F16.wireOp",EDGE,"E87.MirrorCS");Q2=makeQuery(id+"F16.imprint","IMPRINT",FACE,{"disambiguationData":[TD([[makeQuery(id+"F16.imprint","IMPRINT",EDGE,{"derivedFrom":subQ1}),1.0]])]});}
            var Q3;
            Q3=makeQuery(id+"F2.opExtrude","CAP_FACE",FACE,{"disambiguationData":[OSD([sQuery(id+"F0.wireOp",EDGE,"E12"),sQuery(id+"F0.wireOp",EDGE,"E13"),sQuery(id+"F0.wireOp",EDGE,"E14"),sQuery(id+"F0.wireOp",EDGE,"E15"),sQuery(id+"F0.wireOp",EDGE,"E17.filletArc"),sQuery(id+"F0.wireOp",EDGE,"E18.filletArc"),sQuery(id+"F0.wireOp",EDGE,"E19.filletArc"),sQuery(id+"F0.wireOp",EDGE,"E20.filletArc"),sQuery(id+"F0.wireOp",EDGE,"E25.0"),sQuery(id+"F0.wireOp",EDGE,"E25.1"),sQuery(id+"F0.wireOp",EDGE,"E25.2"),sQuery(id+"F0.wireOp",EDGE,"E25.3"),sQuery(id+"F0.wireOp",EDGE,"E25.4"),sQuery(id+"F0.wireOp",EDGE,"E25.5"),sQuery(id+"F0.wireOp",EDGE,"E25.6"),sQuery(id+"F0.wireOp",EDGE,"E25.7")])],"isStart":false});
            extrude(context, id + "F17", {"entities" : qUnion([Q0, Q1, Q2]), "endBound" : BoundingType.UP_TO_SURFACE, "depth" : 25 * mm, "endBoundEntityFace" : qUnion([Q3]), "offsetDistance" : 25 * mm});
        }
    });
